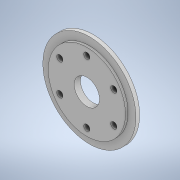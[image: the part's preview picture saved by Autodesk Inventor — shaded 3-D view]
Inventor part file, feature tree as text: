
AUTODESK INVENTOR PART (.ipt)
format: ipt  version: 2022.1 (Build 261234000, 234)  size: 146,944 bytes
history: native  units: in
note: dims shown in document units (in); Inventor stores cm internally (conversion verified against a paired STEP export)
features: sketch x3, extrude x2, hole x1
ambient origin geometry x8: Origin, YZ Plane, XZ Plane, XY Plane, X Axis, Y Axis, Z Axis, Center Point
bodies: Solid1 (feature_tree)
feature tree (6):
  extrude  "Extrusion1"  Depth=3.735in
  extrude  "Extrusion2"  Depth=0.15in
  hole  "Hole2"  [1 undecoded]
  sketch  "Sketch1"  dims[d0=1.015in d1=3.735in]
  sketch  "Sketch2"  dims[d2=0.15in d3=0.0in d4=3.1in]
  sketch  "Sketch4"  dims[d5=0.1in d6=0.0in d19=1.25in d20=2.3622in d22=360.0deg d24=0.218in d25=0.75in d26=0.249in d27=0.1944in d28=0.5635in d29=0.25in d30=0.8108in]
note: 1 required parameter value undecoded (feature->parameter linkage not recoverable at this tier; creation-order binding heuristic only, values carry confidence <= 0.55)
